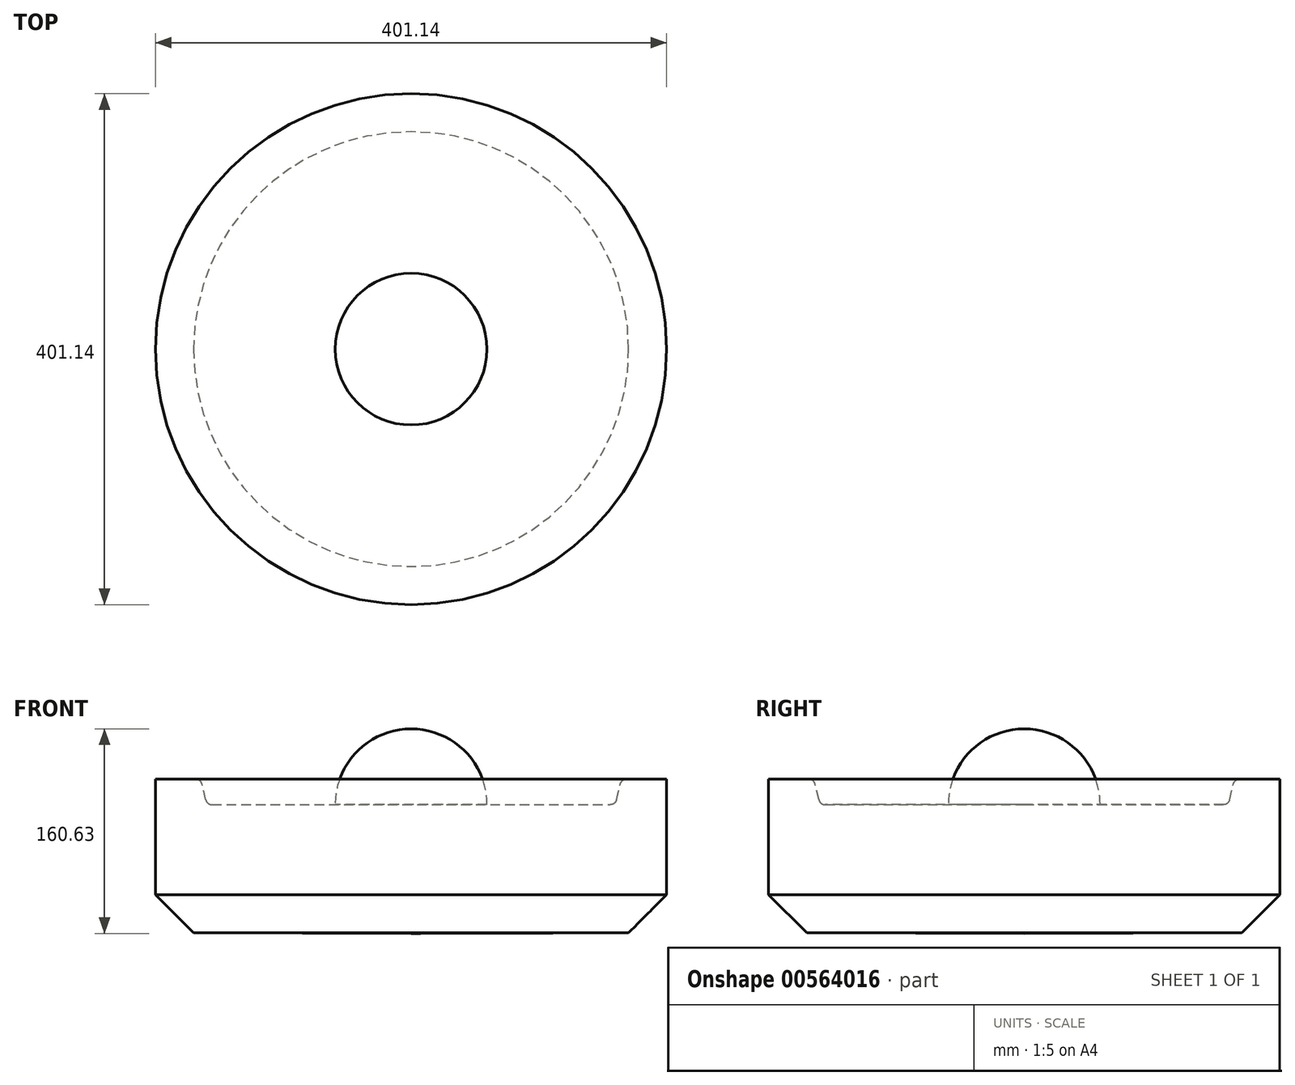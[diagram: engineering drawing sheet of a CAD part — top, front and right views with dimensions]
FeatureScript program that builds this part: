
annotation { "Feature Type Name" : "Feature", "Feature Type Description" : "" }
export const myFeature = defineFeature(function(context is Context, id is Id, definition is map)
    precondition{}
    {
        {
            var Q0;
            Q0=qCreatedBy(makeId("Front.planeOp"),FACE);
            var sketch = newSketch(context, id + "F0", { "sketchPlane" : qUnion([Q0])});
            skLineSegment(sketch, "E0", {"start": v(0, -101.1) * mm, "end": v(0, 0) * mm});
            skLineSegment(sketch, "E1", {"start": v(0, 0) * mm, "end": v(160.2, 0) * mm});
            skLineSegment(sketch, "E2", {"start": v(160.2, 0) * mm, "end": v(165.1, 20.01) * mm});
            skLineSegment(sketch, "E3", {"start": v(165.1, 20.01) * mm, "end": v(200.57, 20.01) * mm});
            skLineSegment(sketch, "E4", {"start": v(200.57, 20.01) * mm, "end": v(200.57, -100.5) * mm});
            skLineSegment(sketch, "E5", {"start": v(200.57, -100.5) * mm, "end": v(0, -101.1) * mm});
            skSolve(sketch);
        }
        {
            var Q0;
            Q0=makeQuery(id+"F0.imprint","IMPRINT",FACE,{"disambiguationData":[TD([[makeQuery(id+"F0.imprint","IMPRINT",EDGE,{"derivedFrom":sQuery(id+"F0.wireOp",EDGE,"E0")}),-1.0]])]});
            var Q1;
            Q1=sQuery(id+"F0.wireOp",EDGE,"E0");
            revolve(context, id + "F1", {"entities" : qUnion([Q0]), "axis" : qUnion([Q1]), "revolveType" : RevolveType.FULL});
        }
        {
            var Q0;
            Q0=makeQuery(id+"F1.opRevolve","SWEPT_EDGE",EDGE,{"disambiguationData":[OSD([sQuery(id+"F0.wireOp",EDGE,"E4"),sQuery(id+"F0.wireOp",EDGE,"E5")])]});
            chamfer(context, id + "F2", {"entities" : qUnion([Q0]), "width" : 30 * mm, "tangentPropagation" : true});
        }
        {
            var Q0;
            Q0=qCreatedBy(makeId("Front.planeOp"),FACE);
            var sketch = newSketch(context, id + "F3", { "sketchPlane" : qUnion([Q0])});
            skArc(sketch, "E6", {"start": v(59.53, 0) * mm, "mid": v(0, 59.53) * mm, "end": v(-59.53, 0) * mm});
            skLineSegment(sketch, "E7", {"start": v(0, 0) * mm, "end": v(-59.53, 0) * mm});
            skLineSegment(sketch, "E8", {"start": v(0, 0) * mm, "end": v(59.53, 0) * mm});
            skSolve(sketch);
        }
        {
            var Q0;
            Q0 = qSketchRegion(id + "F3", true);
            var Q1;
            Q1=sQuery(id+"F3.wireOp",EDGE,"E7");
            revolve(context, id + "F4", {"operationType" : NewBodyOperationType.ADD, "entities" : qUnion([Q0]), "axis" : qUnion([Q1]), "revolveType" : RevolveType.FULL});
        }
        {
            var Q0;
            Q0=makeQuery(id+"F1.opRevolve","SWEPT_EDGE",EDGE,{"disambiguationData":[OSD([sQuery(id+"F0.wireOp",EDGE,"E2"),sQuery(id+"F0.wireOp",EDGE,"E3")])]});
            var Q1;
            Q1=makeQuery(id+"F1.opRevolve","SWEPT_EDGE",EDGE,{"disambiguationData":[OSD([sQuery(id+"F0.wireOp",EDGE,"E1"),sQuery(id+"F0.wireOp",EDGE,"E2")])]});
            fillet(context, id + "F5", {"entities" : qUnion([Q0, Q1]), "radius" : 5 * mm, "tangentPropagation" : true, "allowEdgeOverflow" : false});
        }
    });
